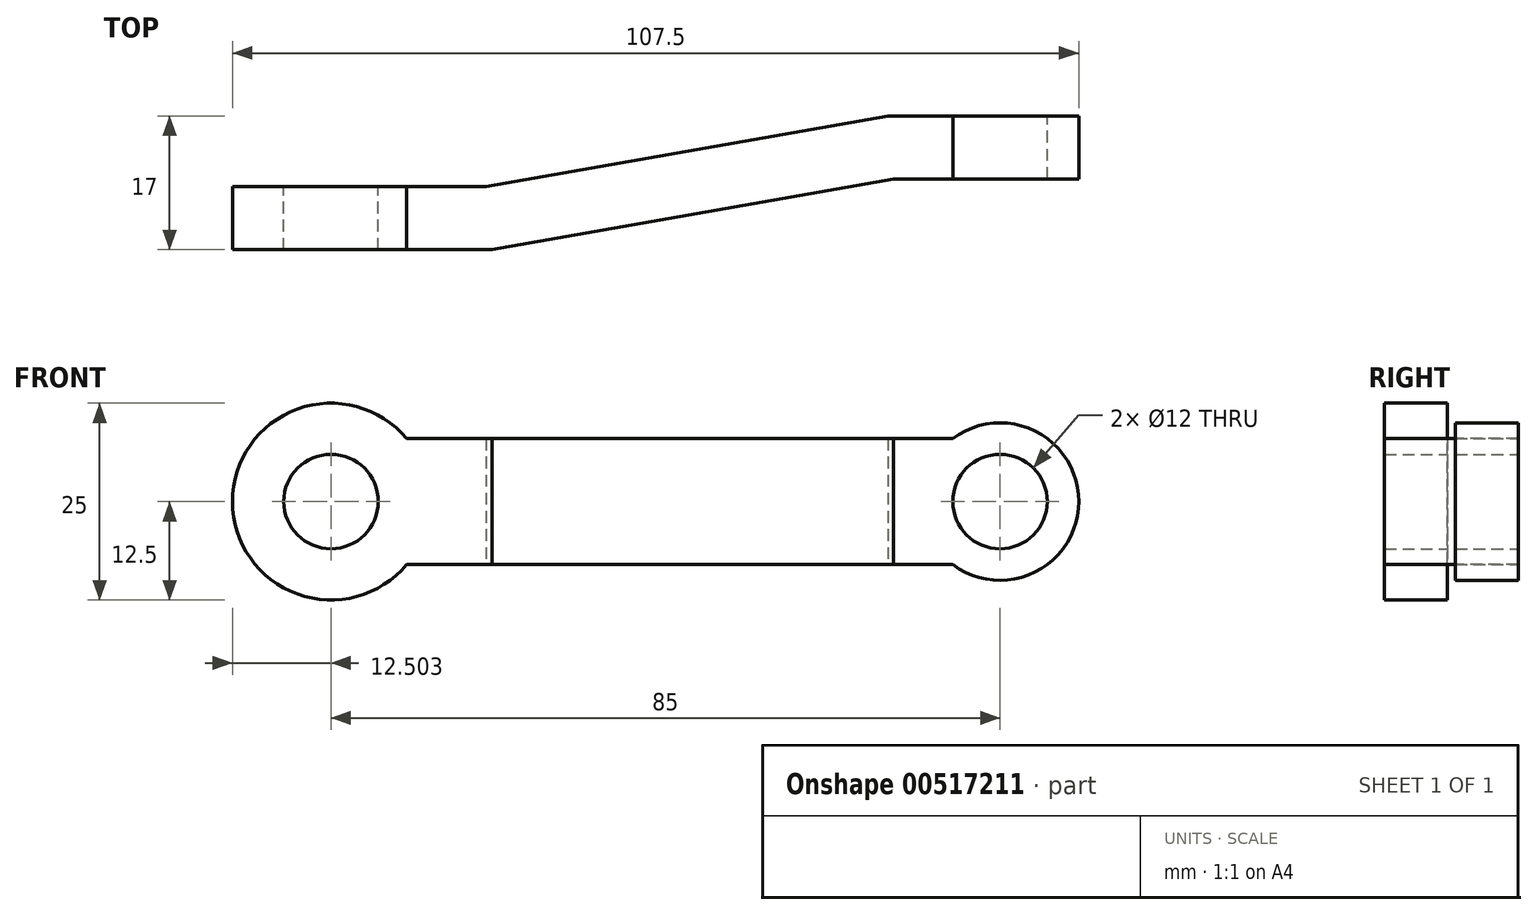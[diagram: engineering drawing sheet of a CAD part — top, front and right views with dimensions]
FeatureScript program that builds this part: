
annotation { "Feature Type Name" : "Feature", "Feature Type Description" : "" }
export const myFeature = defineFeature(function(context is Context, id is Id, definition is map)
    precondition{}
    {
        {
            var Q0;
            Q0=qCreatedBy(makeId("Front.planeOp"),FACE);
            var sketch = newSketch(context, id + "F0", { "sketchPlane" : qUnion([Q0])});
            skArc(sketch, "E0", {"start": v(-29.3, 8) * mm, "mid": v(-51.4, 0) * mm, "end": v(-29.3, -8) * mm});
            skArc(sketch, "E1", {"start": v(40.1, -8) * mm, "mid": v(56.1, 0) * mm, "end": v(40.1, 8) * mm});
            skLineSegment(sketch, "E2", {"start": v(-29.3, 8) * mm, "end": v(40.1, 8) * mm});
            skLineSegment(sketch, "E3.MirrorCS", {"start": v(-29.3, -8) * mm, "end": v(40.1, -8) * mm});
            skCircle(sketch, "E4", {"center": v(-38.9, 0) * mm, "radius": 6 * mm});
            skCircle(sketch, "E5", {"center": v(46.1, 0) * mm, "radius": 6 * mm});
            skSolve(sketch);
        }
        {
            var Q0;
            Q0=makeQuery(id+"F0.imprint","IMPRINT",FACE,{"disambiguationData":[TD([[makeQuery(id+"F0.imprint","IMPRINT",EDGE,{"derivedFrom":sQuery(id+"F0.wireOp",EDGE,"E0")}),1.0]])]});
            extrude(context, id + "F1", {"entities" : qUnion([Q0]), "depth" : 25 * mm, "offsetDistance" : 25 * mm});
        }
        {
            var Q0;
            Q0=qCreatedBy(makeId("Top.planeOp"),FACE);
            var sketch = newSketch(context, id + "F2", { "sketchPlane" : qUnion([Q0])});
            skLineSegment(sketch, "E6", {"start": v(-51.4, -9) * mm, "end": v(-19.16, -9) * mm});
            skLineSegment(sketch, "E7", {"start": v(-19.16, -9) * mm, "end": v(31.88, 0) * mm});
            skLineSegment(sketch, "E8", {"start": v(31.88, 0) * mm, "end": v(56.1, 0) * mm});
            skLineSegment(sketch, "E9.0", {"start": v(-18.46, -17) * mm, "end": v(32.58, -8) * mm});
            skLineSegment(sketch, "E9.1", {"start": v(-51.4, -17) * mm, "end": v(-18.46, -17) * mm});
            skLineSegment(sketch, "E10.0", {"start": v(32.58, -8) * mm, "end": v(56.1, -8) * mm});
            skLineSegment(sketch, "E11", {"start": v(-51.4, -25) * mm, "end": v(-51.4, 0) * mm});
            skLineSegment(sketch, "E12", {"start": v(56.1, 0) * mm, "end": v(56.1, -25) * mm});
            skSolve(sketch);
        }
        {
            var Q0;
            Q0 = qSketchRegion(id + "F2", true);
            extrude(context, id + "F3", {"entities" : qUnion([Q0]), "operationType" : NewBodyOperationType.INTERSECT, "endBound" : BoundingType.SYMMETRIC, "depth" : 25 * mm, "offsetDistance" : 25 * mm});
        }
    });
